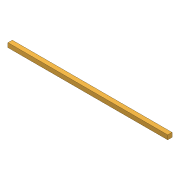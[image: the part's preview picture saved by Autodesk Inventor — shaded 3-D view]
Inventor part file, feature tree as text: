
AUTODESK INVENTOR PART (.ipt)
format: ipt  version: 2021 (Build 250183000, 183)  size: 76,800 bytes
history: native  units: in
note: dims shown in document units (in); Inventor stores cm internally (conversion verified against a paired STEP export)
features: extrude x1, sketch x1
ambient origin geometry x8: Origin, YZ Plane, XZ Plane, XY Plane, X Axis, Y Axis, Z Axis, Center Point
bodies: Solid1 (feature_tree)
feature tree (2):
  extrude  "Extrusion1"  Depth=0.0625in
  sketch  "Sketch1"  dims[d0=2.3125in d1=0.0in d2=0.0625in d3=0.0625in]
